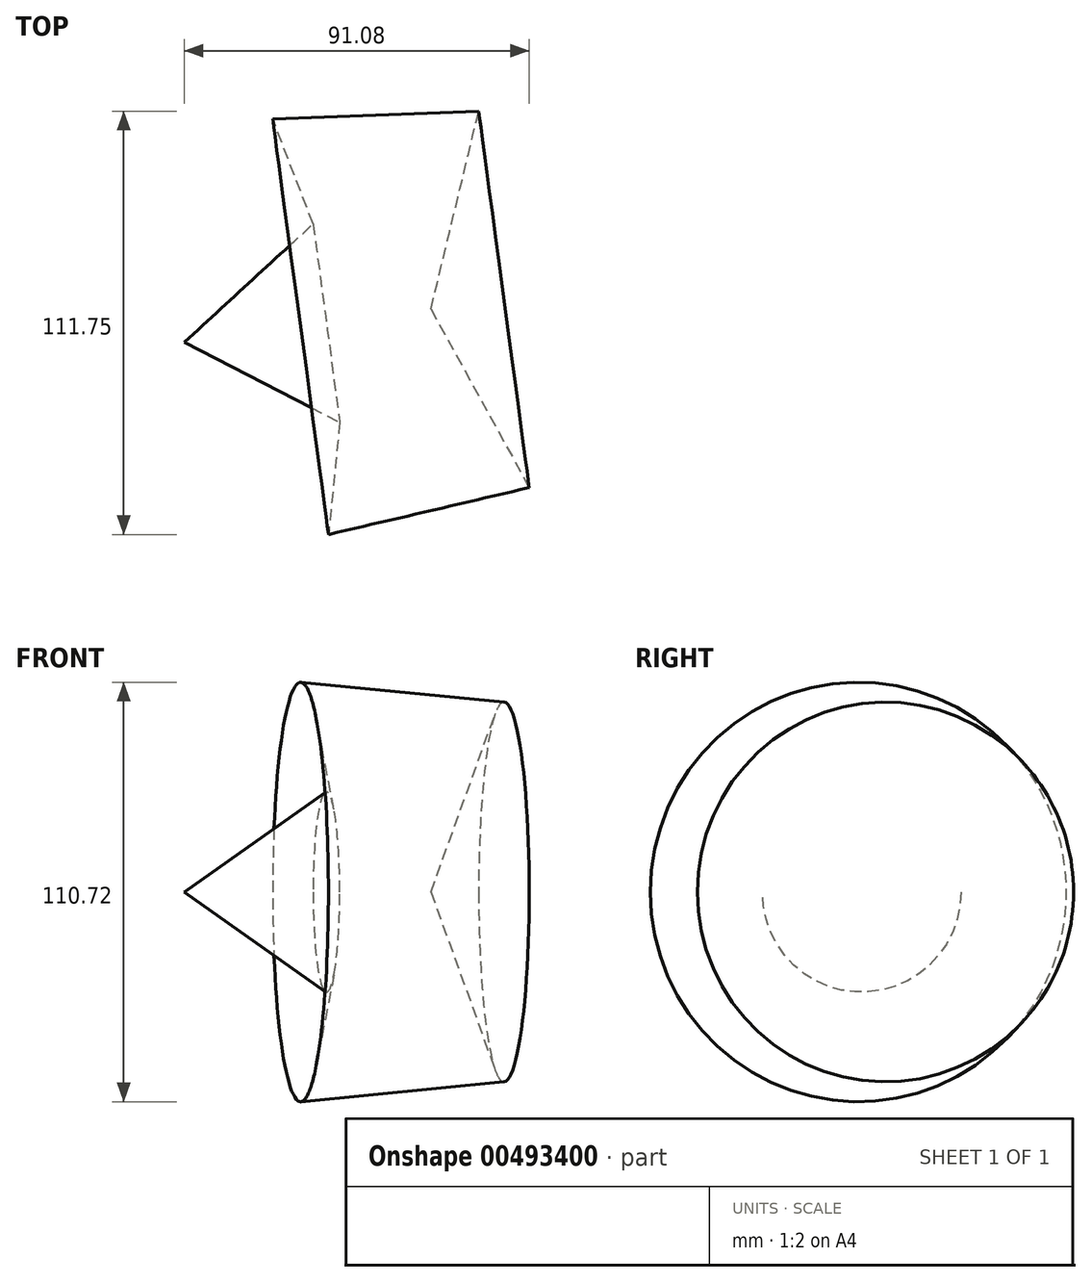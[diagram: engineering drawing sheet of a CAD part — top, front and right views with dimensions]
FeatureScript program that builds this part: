
annotation { "Feature Type Name" : "Feature", "Feature Type Description" : "" }
export const myFeature = defineFeature(function(context is Context, id is Id, definition is map)
    precondition{}
    {
        {
            var Q0;
            Q0=qCreatedBy(makeId("Top.planeOp"),FACE);
            var sketch = newSketch(context, id + "F0", { "sketchPlane" : qUnion([Q0])});
            skLineSegment(sketch, "E0", {"start": v(0, 0) * mm, "end": v(-41.05, 21.17) * mm});
            skLineSegment(sketch, "E1", {"start": v(-41.05, 21.17) * mm, "end": v(24.09, 29.91) * mm});
            skLineSegment(sketch, "E2", {"start": v(24.09, 29.91) * mm, "end": v(50.03, -17.18) * mm});
            skLineSegment(sketch, "E3", {"start": v(50.03, -17.18) * mm, "end": v(-2.98, -29.58) * mm});
            skLineSegment(sketch, "E4", {"start": v(-2.98, -29.58) * mm, "end": v(0, 0) * mm});
            skSolve(sketch);
        }
        {
            var Q0;
            Q0=makeQuery(id+"F0.imprint","IMPRINT",FACE,{"disambiguationData":[TD([[makeQuery(id+"F0.imprint","IMPRINT",EDGE,{"derivedFrom":sQuery(id+"F0.wireOp",EDGE,"E0")}),-1.0]])]});
            var Q1;
            Q1=sQuery(id+"F0.wireOp",EDGE,"E1");
            revolve(context, id + "F1", {"entities" : qUnion([Q0]), "axis" : qUnion([Q1]), "revolveType" : RevolveType.FULL});
        }
    });
